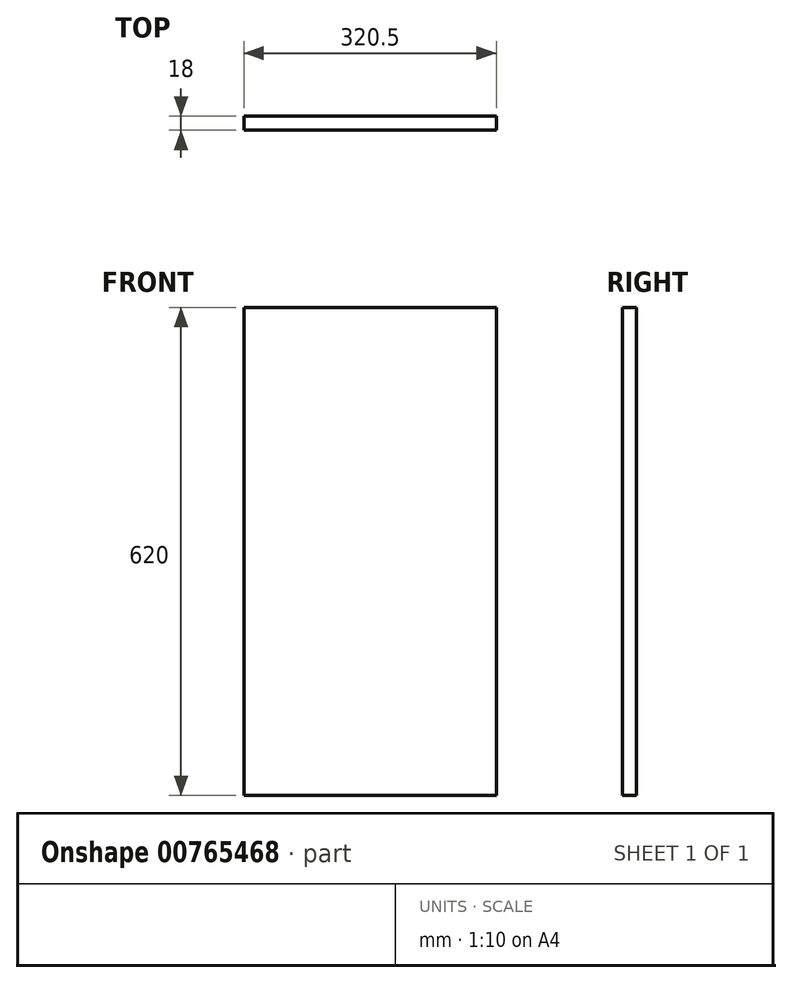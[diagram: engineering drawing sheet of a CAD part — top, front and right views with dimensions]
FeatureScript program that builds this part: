
annotation { "Feature Type Name" : "Feature", "Feature Type Description" : "" }
export const myFeature = defineFeature(function(context is Context, id is Id, definition is map)
    precondition{}
    {
        {
            var Q0;
            Q0=qCreatedBy(makeId("Front.planeOp"),FACE);
            var sketch = newSketch(context, id + "F0", { "sketchPlane" : qUnion([Q0])});
            skLineSegment(sketch, "E0.bottom", {"start": v(-160.25, -310) * mm, "end": v(160.25, -310) * mm});
            skLineSegment(sketch, "E0.top", {"start": v(-160.25, 310) * mm, "end": v(160.25, 310) * mm});
            skLineSegment(sketch, "E0.left", {"start": v(-160.25, -310) * mm, "end": v(-160.25, 310) * mm});
            skLineSegment(sketch, "E0.right", {"start": v(160.25, -310) * mm, "end": v(160.25, 310) * mm});
            skPoint(sketch, "E0.middle", {"position": v(0, 0) * mm});
            skSolve(sketch);
        }
        {
            var Q0;
            Q0 = qSketchRegion(id + "F0", true);
            extrude(context, id + "F1", {"entities" : qUnion([Q0]), "depth" : 18 * mm, "offsetDistance" : 25 * mm});
        }
    });
